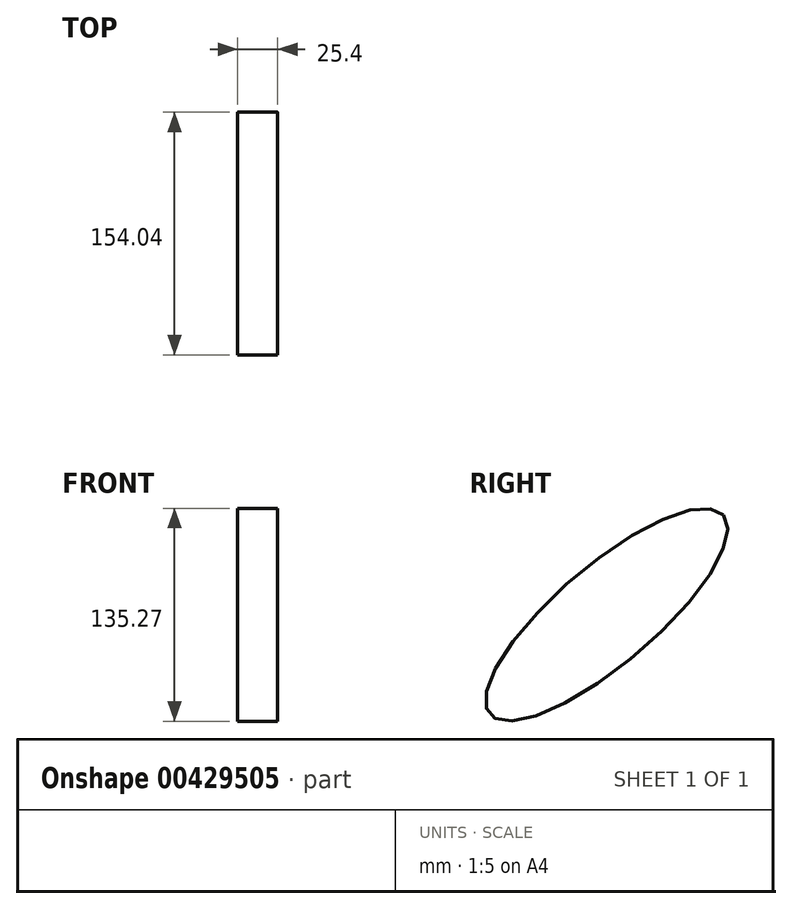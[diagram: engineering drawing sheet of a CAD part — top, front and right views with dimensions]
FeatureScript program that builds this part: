
annotation { "Feature Type Name" : "Feature", "Feature Type Description" : "" }
export const myFeature = defineFeature(function(context is Context, id is Id, definition is map)
    precondition{}
    {
        {
            var Q0;
            Q0=qCreatedBy(makeId("Right.planeOp"),FACE);
            var sketch = newSketch(context, id + "F0", { "sketchPlane" : qUnion([Q0])});
            skEllipse(sketch, "E0", {"center": v(-51.35, -27.05) * mm, "majorRadius": 97.6 * mm, "minorRadius": 31.3 * mm, "majorAxis": v(0.76, 0.65)});
            skSolve(sketch);
        }
        {
            var Q0;
            Q0 = qSketchRegion(id + "F0", true);
            extrude(context, id + "F1", {"entities" : qUnion([Q0]), "depth" : 25.4 * mm});
        }
    });
